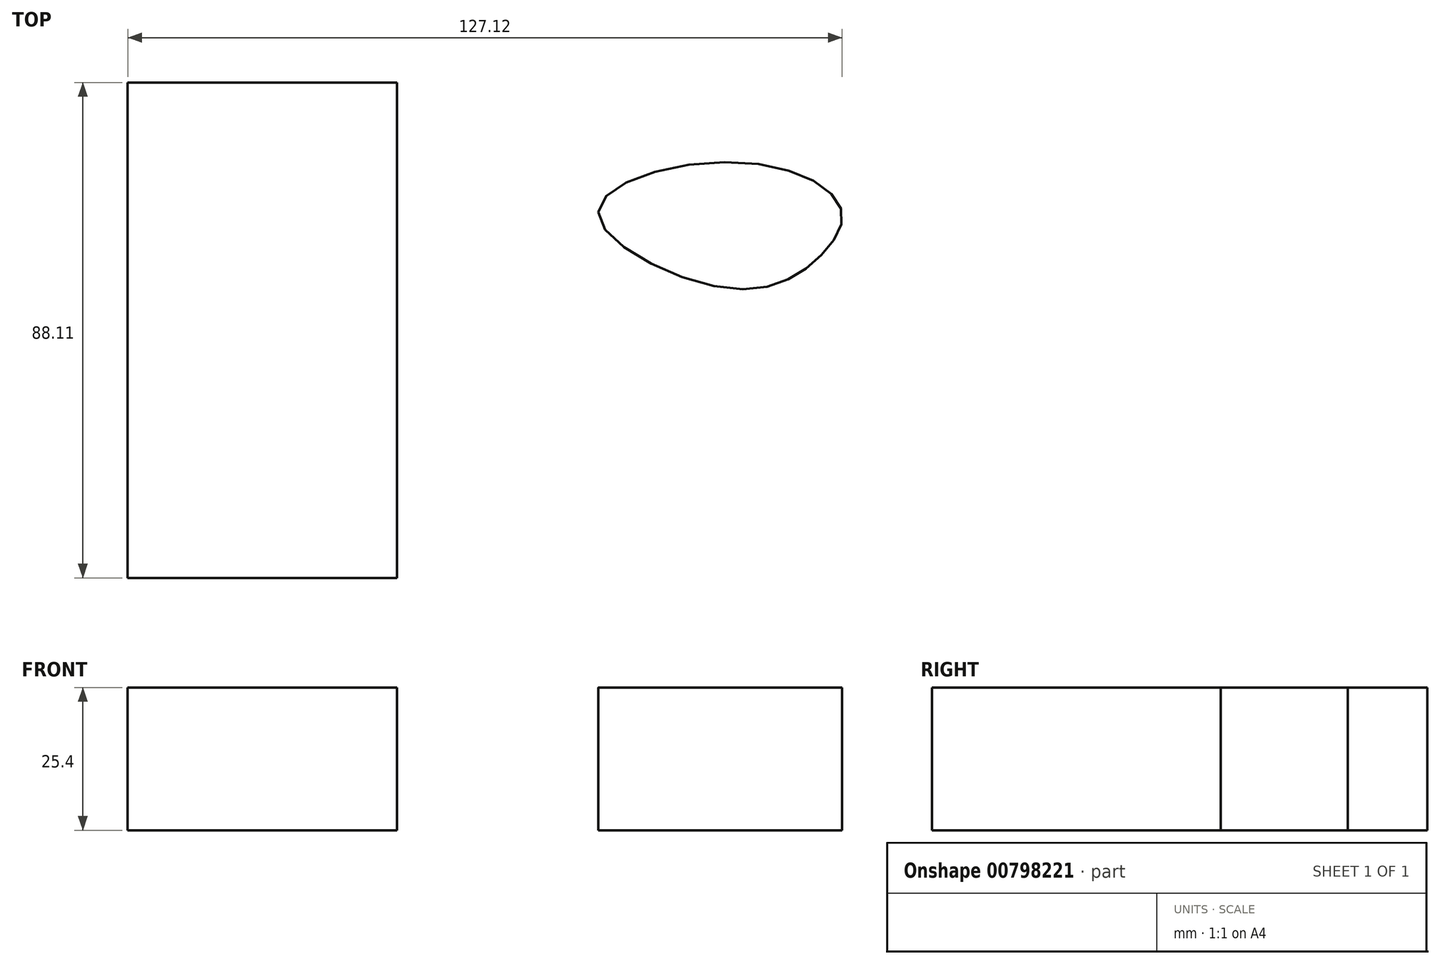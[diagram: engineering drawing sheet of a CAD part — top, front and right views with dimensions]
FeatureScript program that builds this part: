
annotation { "Feature Type Name" : "Feature", "Feature Type Description" : "" }
export const myFeature = defineFeature(function(context is Context, id is Id, definition is map)
    precondition{}
    {
        {
            var Q0;
            Q0=qCreatedBy(makeId("Top.planeOp"),FACE);
            var sketch = newSketch(context, id + "F0", { "sketchPlane" : qUnion([Q0])});
            skLineSegment(sketch, "E0.bottom", {"start": v(-130.53, 54.82) * mm, "end": v(-82.6, 54.82) * mm});
            skLineSegment(sketch, "E0.top", {"start": v(-130.53, -33.3) * mm, "end": v(-82.6, -33.3) * mm});
            skLineSegment(sketch, "E0.left", {"start": v(-130.53, 54.82) * mm, "end": v(-130.53, -33.3) * mm});
            skLineSegment(sketch, "E0.right", {"start": v(-82.6, 54.82) * mm, "end": v(-82.6, -33.3) * mm});
            skFitSpline(sketch, "E1", {"points": [v(-46.8, 31.8) * mm, v(-22.32, 40.66) * mm, v(-3.6, 32.28) * mm, v(-8.03, 23.25) * mm, v(-24.46, 18.32) * mm, v(-46.8, 31.8) * mm]});
            skSolve(sketch);
        }
        {
            var Q0;
            Q0=makeQuery(id+"F0.imprint","IMPRINT",FACE,{"disambiguationData":[TD([[makeQuery(id+"F0.imprint","IMPRINT",EDGE,{"derivedFrom":sQuery(id+"F0.wireOp",EDGE,"E0.bottom")}),-1.0]])]});
            extrude(context, id + "F1", {"entities" : qUnion([Q0]), "depth" : 25.4 * mm, "offsetDistance" : 25.4 * mm});
        }
        {
            var Q0;
            Q0=makeQuery(id+"F0.imprint","IMPRINT",FACE,{"disambiguationData":[TD([[makeQuery(id+"F0.imprint","IMPRINT",EDGE,{"derivedFrom":sQuery(id+"F0.wireOp",EDGE,"E1")}),-1.0]])]});
            extrude(context, id + "F2", {"entities" : qUnion([Q0]), "depth" : 25.4 * mm, "offsetDistance" : 25.4 * mm});
        }
    });
